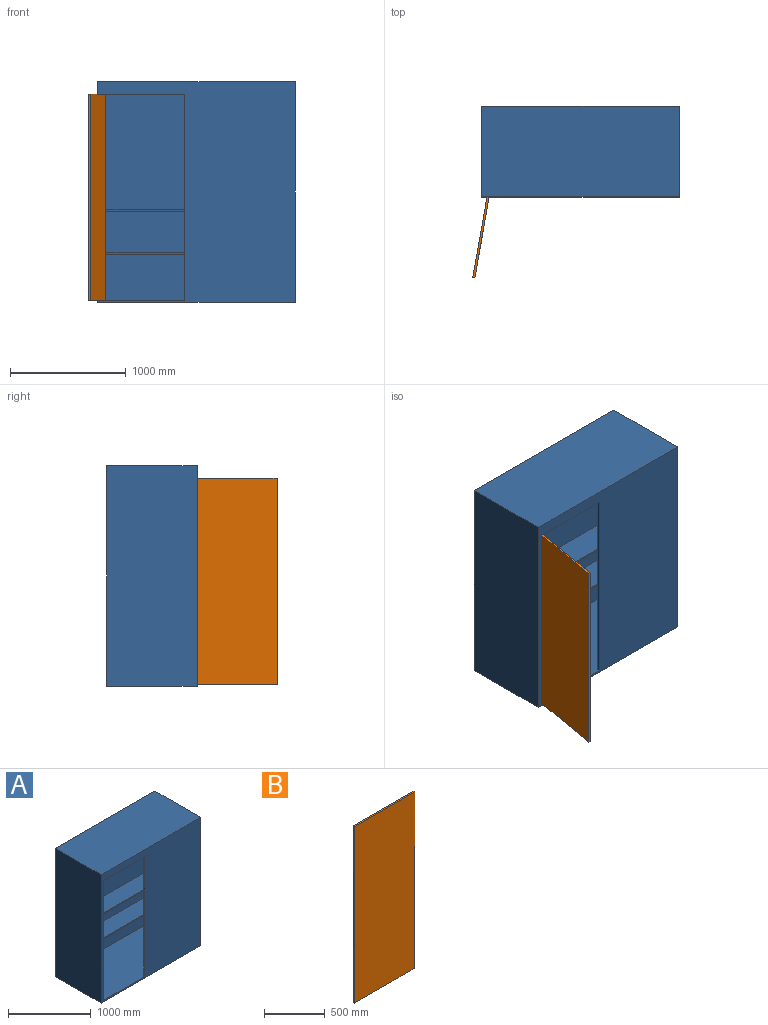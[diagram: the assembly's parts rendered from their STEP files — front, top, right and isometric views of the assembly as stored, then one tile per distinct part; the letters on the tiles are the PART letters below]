
ASSEMBLY  parts=2 mates=1
PART A: 50 faces, bbox 1700x780x1900 mm
  f0: plane 1776x912mm, normal (0,1,0), area 1610332.5mm2, adj f9,f21,f24,f25,f26,f27,f28,f29
  f1: plane 604x26mm, normal (0,0,-1), area 15704mm2, adj f4,f21,f33,f43
  f2: plane 604x396mm, normal (-1,0,0), area 239184mm2, adj f24,f25,f35,f47
  f3: plane 604x350mm, normal (-1,0,0), area 211400mm2, adj f27,f28,f37,f44
  f4: plane 994x604mm, normal (-1,0,0), area 600376mm2, adj f1,f30,f33,f43
  f5: plane 1612x26mm, normal (0,0,-1), area 41912mm2, adj f8,f19,f20,f21
  f6: plane 1612x350mm, normal (0,-1,0), area 564200mm2, adj f27,f28,f39,f45
  f7: plane 1612x396mm, normal (0,-1,0), area 638352mm2, adj f24,f25,f42,f46
  f8: plane 1612x994mm, normal (0,-1,0), area 1600364.5mm2, adj f5,f19,f21,f30,f31
  f9: plane 1612x44mm, normal (0,0,-1), area 54512mm2, adj f0,f12,f18,f19,f21,f48
  f10: plane 1776x604mm, normal (1,0,0), area 1066224mm2, adj f17,f22,f23,f24,f25,f27,f28,f30
  f11: plane 1900x780mm, normal (-1,0,0), area 1482000mm2, adj f12,f14,f15,f16
  f12: plane 1900x1700mm, normal (0,-1,0), area 1986800mm2, adj f9,f11,f13,f15,f16,f19,f24,f48
  f13: plane 1900x780mm, normal (1,0,0), area 1482000mm2, adj f12,f14,f15,f16
  f14: plane 1900x1700mm, normal (0,1,0), area 3230000mm2, adj f11,f13,f15,f16
  f15: plane 1700x780mm, normal (0,0,1), area 1326000mm2, adj f11,f12,f13,f14
  f16: plane 1700x780mm, normal (0,0,-1), area 1326000mm2, adj f11,f12,f13,f14
  f17: plane 604x26mm, normal (0,0,-1), area 15704mm2, adj f10,f19,f32,f38
  f18: plane 1612x88mm, normal (0,1,0), area 141856mm2, adj f9,f19,f21,f49
  f19: plane 1864x762mm, normal (1,0,0), area 286764mm2, adj f5,f8,f9,f12,f17,f18,f20,f24
  f20: plane 1612x88mm, normal (0,-1,0), area 141856mm2, adj f5,f19,f21,f49
  f21: plane 1082x744mm, normal (-1,0,0), area 200056mm2, adj f0,f1,f5,f8,f9,f18,f20,f30
  f22: plane 1432x18mm, normal (0,-1,0), area 25776mm2, adj f10,f28,f29,f30
  f23: plane 1432x18mm, normal (0,-1,0), area 25776mm2, adj f10,f25,f26,f27
  f24: plane 1664x762mm, normal (0,0,1), area 1243336mm2, adj f0,f2,f7,f10,f12,f19,f32,f34
  f25: plane 1664x744mm, normal (0,0,-1), area 525148mm2, adj f0,f2,f7,f10,f23,f26,f34,f35
  f26: plane 494x18mm, normal (-1,0,0), area 8892mm2, adj f0,f23,f25,f27
  f27: plane 1664x744mm, normal (0,0,1), area 525148mm2, adj f0,f3,f6,f10,f23,f26,f36,f37
  f28: plane 1664x744mm, normal (0,0,-1), area 525148mm2, adj f0,f3,f6,f10,f22,f29,f36,f37
  f29: plane 494x18mm, normal (-1,0,0), area 8892mm2, adj f0,f22,f28,f30
  f30: plane 1664x744mm, normal (0,0,1), area 525148mm2, adj f0,f4,f8,f10,f19,f21,f22,f29
  f31: cylinder r=25mm len=744mm, axis (0,1,0), area 116867.2mm2, adj f0,f8
  f32: plane 1776x26mm, normal (0,1,0), area 46176mm2, adj f10,f17,f19,f24
  f33: plane 994x26mm, normal (0,1,0), area 25844mm2, adj f1,f4,f21,f30
  f34: plane 396x70mm, normal (-1,0,0), area 27720mm2, adj f0,f24,f25,f35
  f35: plane 396x26mm, normal (0,1,0), area 10296mm2, adj f2,f24,f25,f34
  f36: plane 350x70mm, normal (-1,0,0), area 24500mm2, adj f0,f27,f28,f37
  f37: plane 350x26mm, normal (0,1,0), area 9100mm2, adj f3,f27,f28,f36
  f38: plane 994x26mm, normal (0,-1,0), area 25844mm2, adj f10,f17,f19,f30
  f39: plane 350x70mm, normal (1,0,0), area 24500mm2, adj f6,f27,f28,f40
  f40: plane 350x26mm, normal (0,-1,0), area 9100mm2, adj f10,f27,f28,f39
  f41: plane 396x26mm, normal (0,-1,0), area 10296mm2, adj f10,f24,f25,f42
  f42: plane 396x70mm, normal (1,0,0), area 27720mm2, adj f7,f24,f25,f41
  f43: plane 994x26mm, normal (0,-1,0), area 25844mm2, adj f1,f4,f21,f30
  f44: plane 350x26mm, normal (0,-1,0), area 9100mm2, adj f3,f27,f28,f45
  f45: plane 350x70mm, normal (-1,0,0), area 24500mm2, adj f6,f27,f28,f44
  f46: plane 396x70mm, normal (-1,0,0), area 27720mm2, adj f7,f24,f25,f47
  f47: plane 396x26mm, normal (0,-1,0), area 10296mm2, adj f2,f24,f25,f46
  f48: plane 1776x18mm, normal (-1,0,0), area 31968mm2, adj f0,f9,f12,f24
  f49: plane 1612x692mm, normal (0,0,-1), area 1115504mm2, adj f18,f19,f20,f21
PART B: 6 faces, bbox 700x18x1776 mm
  f0: plane 1776x18mm, normal (-1,0,0), area 31968mm2, adj f1,f3,f4,f5
  f1: plane 700x18mm, normal (0,0,-1), area 12600mm2, adj f0,f2,f4,f5
  f2: plane 1776x18mm, normal (1,0,0), area 31968mm2, adj f1,f3,f4,f5
  f3: plane 700x18mm, normal (0,0,1), area 12600mm2, adj f0,f2,f4,f5
  f4: plane 1776x700mm, normal (0,-1,0), area 1243200mm2, adj f0,f1,f2,f3
  f5: plane 1776x700mm, normal (0,1,0), area 1243200mm2, adj f0,f1,f2,f3
PLACE A t=(-1290.87,-424.63,1048.05)mm fixed
PLACE B rot(axis=(0,0,-1),100deg) t=(-1229.14,-427.76,1066.05)mm
MATE revolute B.f1 <-> A.f24  axis (0,0,1) through (-1246.87,-424.63,1066.05)mm
